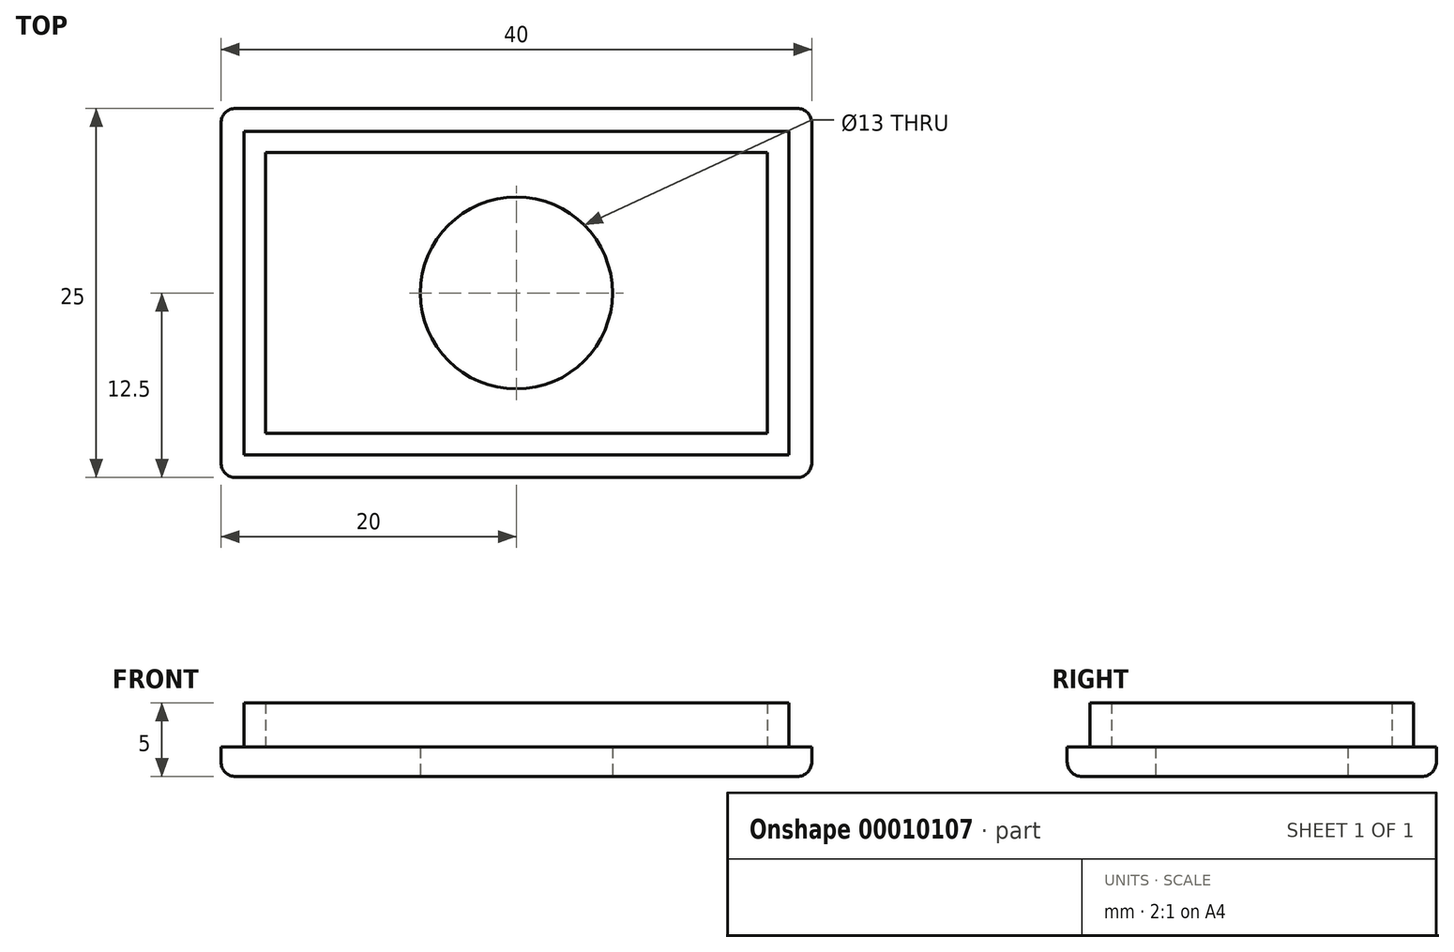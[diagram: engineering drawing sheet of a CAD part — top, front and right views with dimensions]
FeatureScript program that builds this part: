
annotation { "Feature Type Name" : "Feature", "Feature Type Description" : "" }
export const myFeature = defineFeature(function(context is Context, id is Id, definition is map)
    precondition{}
    {
        {
            var Q0;
            Q0=qCreatedBy(makeId("Top.planeOp"),FACE);
            var sketch = newSketch(context, id + "F0", { "sketchPlane" : qUnion([Q0])});
            skLineSegment(sketch, "E0.rect.bottom", {"start": v(20, 12.5) * mm, "end": v(-20, 12.5) * mm});
            skLineSegment(sketch, "E0.rect.top", {"start": v(20, -12.5) * mm, "end": v(-20, -12.5) * mm});
            skLineSegment(sketch, "E0.rect.left", {"start": v(20, 12.5) * mm, "end": v(20, -12.5) * mm});
            skLineSegment(sketch, "E0.rect.right", {"start": v(-20, 12.5) * mm, "end": v(-20, -12.5) * mm});
            skPoint(sketch, "E0.rect.middle", {"position": v(0, 0) * mm});
            skLineSegment(sketch, "E1.rect.bottom", {"start": v(17, 9.5) * mm, "end": v(-17, 9.5) * mm});
            skLineSegment(sketch, "E1.rect.top", {"start": v(17, -9.5) * mm, "end": v(-17, -9.5) * mm});
            skLineSegment(sketch, "E1.rect.left", {"start": v(17, 9.5) * mm, "end": v(17, -9.5) * mm});
            skLineSegment(sketch, "E1.rect.right", {"start": v(-17, 9.5) * mm, "end": v(-17, -9.5) * mm});
            skLineSegment(sketch, "E2", {"start": v(20, -3.98) * mm, "end": v(17, -3.98) * mm, "construction": true});
            skLineSegment(sketch, "E3", {"start": v(16.8, 12.5) * mm, "end": v(16.8, 9.5) * mm, "construction": true});
            skLineSegment(sketch, "E4.rect.bottom", {"start": v(18.45, 10.95) * mm, "end": v(-18.45, 10.95) * mm});
            skLineSegment(sketch, "E4.rect.top", {"start": v(18.45, -10.95) * mm, "end": v(-18.45, -10.95) * mm});
            skLineSegment(sketch, "E4.rect.left", {"start": v(18.45, 10.95) * mm, "end": v(18.45, -10.95) * mm});
            skLineSegment(sketch, "E4.rect.right", {"start": v(-18.45, 10.95) * mm, "end": v(-18.45, -10.95) * mm});
            skLineSegment(sketch, "E5", {"start": v(-17, 7.8) * mm, "end": v(-18.45, 7.8) * mm, "construction": true});
            skLineSegment(sketch, "E6", {"start": v(-10.2, 9.5) * mm, "end": v(-10.2, 10.95) * mm, "construction": true});
            skCircle(sketch, "E7", {"center": v(0, 0) * mm, "radius": 6.5 * mm});
            skSolve(sketch);
        }
        {
            var Q0;
            Q0=makeQuery(id+"F0.imprint","IMPRINT",FACE,{"disambiguationData":[TD([[makeQuery(id+"F0.imprint","IMPRINT",EDGE,{"derivedFrom":sQuery(id+"F0.wireOp",EDGE,"E0.rect.bottom")}),1.0]])]});
            extrude(context, id + "F1", {"entities" : qUnion([Q0]), "depth" : 2 * mm});
        }
        {
            var Q0;
            Q0=makeQuery(id+"F1.opExtrude","CAP_EDGE",EDGE,{"disambiguationData":[OSD([sQuery(id+"F0.wireOp",EDGE,"E0.rect.right")])],"isStart":true});
            var Q1;
            Q1=makeQuery(id+"F1.opExtrude","CAP_EDGE",EDGE,{"disambiguationData":[OSD([sQuery(id+"F0.wireOp",EDGE,"E0.rect.top")])],"isStart":true});
            var Q2;
            Q2=makeQuery(id+"F1.opExtrude","CAP_EDGE",EDGE,{"disambiguationData":[OSD([sQuery(id+"F0.wireOp",EDGE,"E0.rect.bottom")])],"isStart":true});
            var Q3;
            Q3=makeQuery(id+"F1.opExtrude","CAP_EDGE",EDGE,{"disambiguationData":[OSD([sQuery(id+"F0.wireOp",EDGE,"E0.rect.left")])],"isStart":true});
            var Q4;
            Q4=makeQuery(id+"F1.opExtrude","SWEPT_EDGE",EDGE,{"disambiguationData":[OSD([sQuery(id+"F0.wireOp",EDGE,"E0.rect.bottom"),sQuery(id+"F0.wireOp",EDGE,"E0.rect.right")])]});
            var Q5;
            Q5=makeQuery(id+"F1.opExtrude","SWEPT_EDGE",EDGE,{"disambiguationData":[OSD([sQuery(id+"F0.wireOp",EDGE,"E0.rect.bottom"),sQuery(id+"F0.wireOp",EDGE,"E0.rect.left")])]});
            var Q6;
            Q6=makeQuery(id+"F1.opExtrude","SWEPT_EDGE",EDGE,{"disambiguationData":[OSD([sQuery(id+"F0.wireOp",EDGE,"E0.rect.top"),sQuery(id+"F0.wireOp",EDGE,"E0.rect.right")])]});
            var Q7;
            Q7=makeQuery(id+"F1.opExtrude","SWEPT_EDGE",EDGE,{"disambiguationData":[OSD([sQuery(id+"F0.wireOp",EDGE,"E0.rect.top"),sQuery(id+"F0.wireOp",EDGE,"E0.rect.left")])]});
            fillet(context, id + "F2", {"entities" : qUnion([Q0, Q1, Q2, Q3, Q4, Q5, Q6, Q7]), "radius" : 1 * mm, "tangentPropagation" : true, "allowEdgeOverflow" : false});
        }
        {
            var Q0;
            Q0=makeQuery(id+"F0.imprint","IMPRINT",FACE,{"disambiguationData":[TD([[makeQuery(id+"F0.imprint","IMPRINT",EDGE,{"derivedFrom":sQuery(id+"F0.wireOp",EDGE,"E1.rect.bottom")}),1.0]])]});
            var Q1;
            Q1=makeQuery(id+"F0.imprint","IMPRINT",FACE,{"disambiguationData":[TD([[makeQuery(id+"F0.imprint","IMPRINT",EDGE,{"derivedFrom":sQuery(id+"F0.wireOp",EDGE,"E1.rect.bottom")}),-1.0]])]});
            extrude(context, id + "F3", {"entities" : qUnion([Q0, Q1]), "depth" : 2 * mm});
        }
        {
            var Q0;
            Q0=makeQuery(id+"F0.imprint","IMPRINT",FACE,{"disambiguationData":[TD([[makeQuery(id+"F0.imprint","IMPRINT",EDGE,{"derivedFrom":sQuery(id+"F0.wireOp",EDGE,"E1.rect.bottom")}),-1.0]])]});
            extrude(context, id + "F4", {"entities" : qUnion([Q0]), "operationType" : NewBodyOperationType.ADD, "depth" : 5 * mm});
        }
    });
